# Revit family: IS_Strada_K2623_BIM_DE
name_source: partatom
category: Plumbing Fixtures
revit_build: Autodesk Revit MEP 2016 (Build: 20161004_0715(x64)
units: mm (PartAtom-declared; Revit-internal decimal feet)

## family parameters
Always vertical = No
Cut with Voids When Loaded = No
OmniClass Number = 23.45.05.14.17.17
OmniClass Title = Group Showers
Part Type = Normal
Room Calculation Point = No
Round Connector Dimension = Use Diameter
Shared = No
Work Plane-Based = No

## types (2) — shared parameters
Accessories = www.idealstandard.de\ersatzteile
AreaUnits = millimeters
AssetType = Fixed
BIMobject category = Shower trays
BOSUseNativeGeometries = 1
Brand = Ideal Standard
Brand url = http://www.idealstandard.co.uk
CodePerformance = DIN EN 14527, DIN EN 249
ConnectionType = Plumbing
CurrencyUnit = €
CurrentRevision = 1
Date of publishing = 2017_11_20
DurationUnit = year
Edition number = 1
ExpectedLife = 25
Features = STRADA rectangular shower tray 1000x800mm
HasTray = No
IFC Classification = Sanitary Terminal
IfcExportAs = IfcSanitaryTerminalType
IfcExportType = SHOWERS
Installation instructions = http://www.idealstandard.de
InstallationInstructions = www.idealstandard.de\produkte
LinearUnits = millimeters
Manufacturer name = Ideal Standard
ManufacturerURL = www.idealstandard.com
Material = Sanitary Brass
Material main = Acrylic
NBS Reference Code = 35-06-84
NBS Reference Description = Shower Trays
NettWeight = 20 kg
Nominal height = 60
Nominal width = 800
NominalDepth = 1000 mm
NominalHeight = 58 mm
NominalLength = 1000 mm
NominalWidth = 800 mm
OmniClass Code = 23-31 17 00
OmniClass Description = Showers
Product Guid = 9898a62b-2397-47b9-8187-589439656c39
Product SKU = K2623
Product certification = DIN EN 14527, DIN EN 249
Product data url = https://bimobject.com
Product family = STRADA
Product group = Shower Tray
Product name = STRADA rectangular shower tray 1000x800mm
Product url = http://www.idealstandard.de
ProductInformation = www.idealstandard.de/produkte
QR code = http://bimobject.com
Shape = Rectangular
Size = 800x1000x58 mm
Space = Internal
SpareParts = www.idealstandard.de/ersatzteile
Technical description = http://www.idealstandard.de
URL = http://www.idealstandard.de
Uniclass 1.4 Code = L7214
Uniclass 1.4 Description = Showers
Uniclass 2.0 Code = PR-35-06-84
Uniclass 2.0 Description = Shower Trays
Uniclass 2015 Code = Pr_40_20_06_84
Uniclass 2015 Name = Shower trays
Uniclass2015Code = Pr_40_20_06_84
Uniclass2015Title = Shower trays
Uniclass2015Version = Products v1.1
Version = 1
VolumeUnits = Litres
Weight Net (Kg) = 20
zero-valued in all types: Cost, DrainSize

## per-type parameters (varying)
| type | BIMObjectName | BarCode | Color | EAN code | Finish | MainColor | Model | ModelNumber | Name |
| K262301 STRADA rectangular shower tray 1000x800mm | ISI_IdealStandard_ShowerTrays_Strada_K262301 | 4015413051729 | White | 4015413051729 | White | White | K262301 | K262301 | ShowerTrays_Strada_K262301_IdealStandard |
| K2623YK STRADA rectangular shower tray 1000x800mm | ISI_IdealStandard_ShowerTrays_Strada_K2623YK | 4015413048187 | White Ideal Grip | 4015413048187 | White Ideal Grip | White Ideal Grip | K2623YK | K2623YK | ShowerTrays_Strada_K2623YK_IdealStandard |

note: column(s) folded — value = type name in every type: Description, ModelReference

## geometry (parser evidence)
native form markers: Blend x4, Sweep x2
no freeform markers — native parametric forms only
